# Revit family: RLV-CX_Angle_DN15_RFA
name_source: partatom
category: Pipe Accessories
units: mm (PartAtom-declared; Revit-internal decimal feet)

## family parameters
Always vertical = Yes
Cut with Voids When Loaded = No
OmniClass Number = 23.65.55.14.17
OmniClass Title = Adjusting/Controlling Valves for Liquid Services
Part Type = Valve - Breaks Into
Round Connector Dimension = Use Diameter
Shared = No
Work Plane-Based = No

## types (1)
- RLV-CX_Angle_DN15_003L0273
    D = 15 mm  [stored 0.0492126 ft]
    D1 = 10 mm  [stored 0.0328084 ft]
    DT = 24.6 mm
    Description = Lockshield Valve
    H1 = 27.5 mm  [stored 0.0902231 ft]
    H2 = 22 mm  [stored 0.0721785 ft]
    H3 = 10.2 mm  [stored 0.0334646 ft]
    H3_2 = 26 mm
    H4 = 7 mm  [stored 0.0229659 ft]
    H5 = 6 mm  [stored 0.019685 ft]
    H6 = 8.2 mm  [stored 0.0269029 ft]
    H7 = 12.7 mm  [stored 0.0416667 ft]
    IfcExportAs = IfcValveType
    IfcExportType = RLV-CX
    Kvs = 2.5 m³/h
    L1 = 19.6 mm  [stored 0.0643045 ft]
    L2 = 4 mm  [stored 0.0131234 ft]
    L3 = 10 mm  [stored 0.0328084 ft]
    LL = 57.5 mm  [stored 0.188648 ft]
    LOD 200 = No
    LOD 350 = Yes
    Manufacturer = Danfoss
    Max Medium Temperature = 120 °C
    Max Operating Pressure = 10 bar
    Model = 003L0273
    Model Type = RLV-CX_Angle_DN15
    R1 = 13.25 mm  [stored 0.0434711 ft]
    R2 = 10.5 mm  [stored 0.0344488 ft]
    R3 = 11.64 mm  [stored 0.038189 ft]
    RV2 = 10.5 mm  [stored 0.0344488 ft]
    RV3 = 13.1 mm  [stored 0.042979 ft]
    RV4 = 14.8 mm  [stored 0.0485564 ft]
    RV5 = 10.5 mm  [stored 0.0344488 ft]
    RV_200 = 17.3 mm  [stored 0.0567585 ft]
    R_200 = 15.5 mm  [stored 0.050853 ft]
    URL = https://store.danfoss.com
    Valve Body Material = Danfoss Brass (Chrome plated)
    WN1 = 15.42 mm  [stored 0.0505906 ft]
    WN2 = 17.32 mm
    W_Nut1 = 13.35 mm
    W_Nut2 = 15 mm  [stored 0.0492126 ft]
    Weight = 0.22 kg

note: [stored X ft] marks values corroborated as IEEE doubles in the binary element streams (Revit-internal decimal feet)

## geometry (parser evidence)
native form markers: Sweep x4
no freeform markers — native parametric forms only
